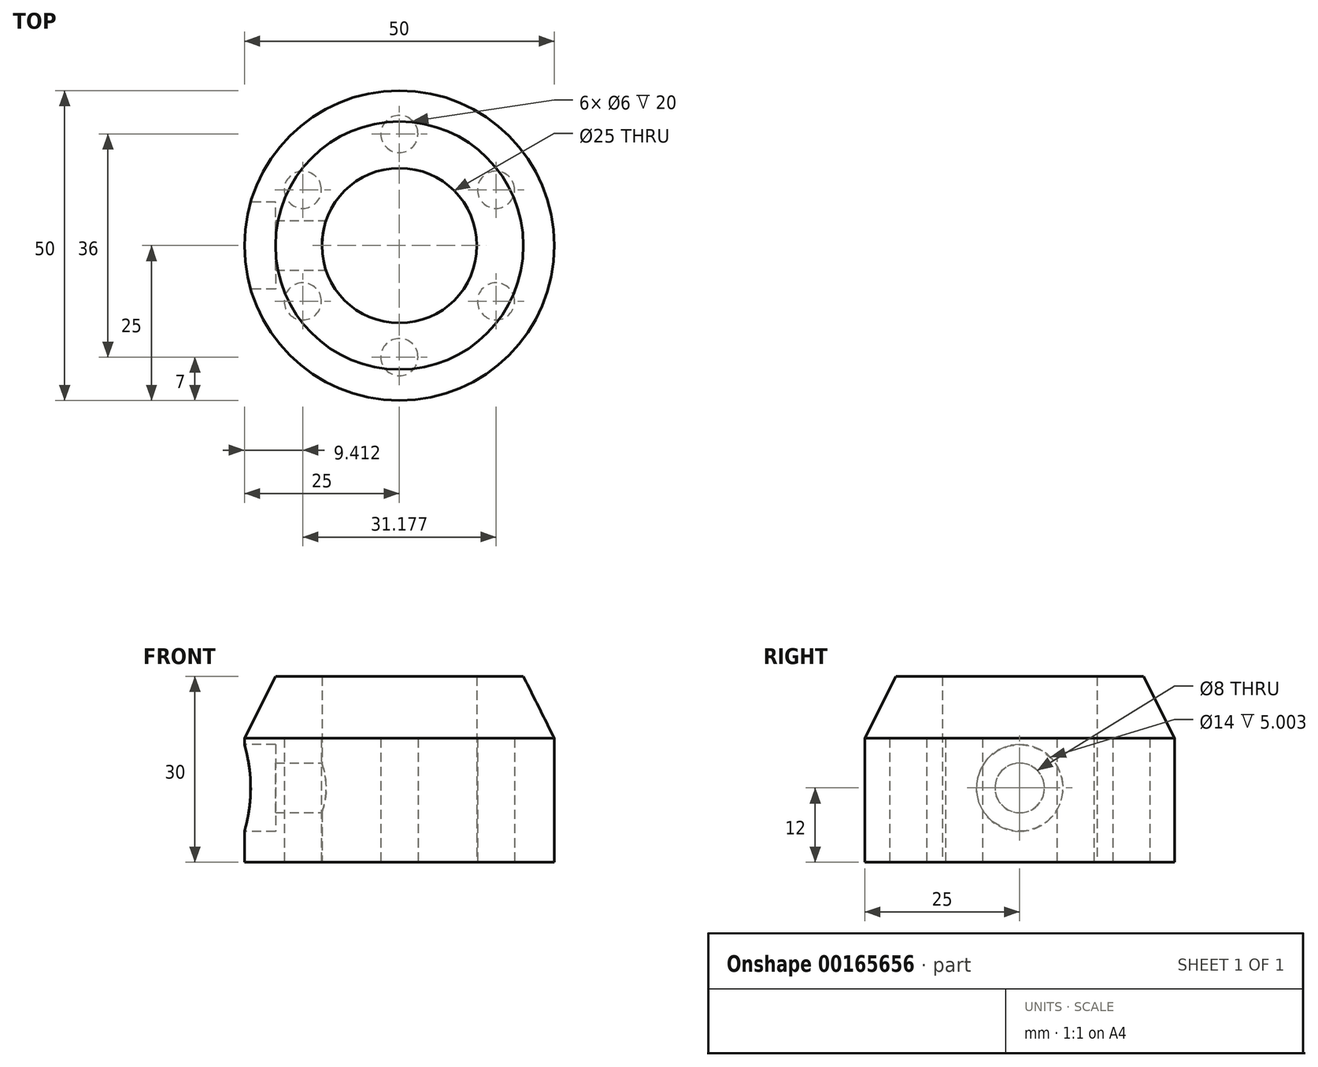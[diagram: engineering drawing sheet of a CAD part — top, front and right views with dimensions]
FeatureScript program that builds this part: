
annotation { "Feature Type Name" : "Feature", "Feature Type Description" : "" }
export const myFeature = defineFeature(function(context is Context, id is Id, definition is map)
    precondition{}
    {
        {
            var Q0;
            Q0=qCreatedBy(makeId("Top.planeOp"),FACE);
            var sketch = newSketch(context, id + "F0", { "sketchPlane" : qUnion([Q0])});
            skCircle(sketch, "E0", {"center": v(0, 0) * mm, "radius": 25 * mm});
            skCircle(sketch, "E1", {"center": v(0, 0) * mm, "radius": 12.5 * mm});
            skCircle(sketch, "E2", {"center": v(0, -18) * mm, "radius": 3 * mm});
            skCircle(sketch, "E3.1.0", {"center": v(15.59, -9) * mm, "radius": 3 * mm});
            skCircle(sketch, "E3.2.0", {"center": v(15.59, 9) * mm, "radius": 3 * mm});
            skCircle(sketch, "E3.3.0", {"center": v(0, 18) * mm, "radius": 3 * mm});
            skCircle(sketch, "E3.4.0", {"center": v(-15.59, 9) * mm, "radius": 3 * mm});
            skCircle(sketch, "E3.5.0", {"center": v(-15.59, -9) * mm, "radius": 3 * mm});
            skSolve(sketch);
        }
        {
            var Q0;
            Q0=makeQuery(id+"F0.imprint","IMPRINT",FACE,{"disambiguationData":[TD([[makeQuery(id+"F0.imprint","IMPRINT",EDGE,{"derivedFrom":sQuery(id+"F0.wireOp",EDGE,"E0")}),1.0]])]});
            var Q1;
            Q1=makeQuery(id+"F0.imprint","IMPRINT",FACE,{"disambiguationData":[TD([[makeQuery(id+"F0.imprint","IMPRINT",EDGE,{"derivedFrom":sQuery(id+"F0.wireOp",EDGE,"E2")}),1.0]])]});
            var Q2;
            Q2=makeQuery(id+"F0.imprint","IMPRINT",FACE,{"disambiguationData":[TD([[makeQuery(id+"F0.imprint","IMPRINT",EDGE,{"derivedFrom":sQuery(id+"F0.wireOp",EDGE,"E3.5.0")}),1.0]])]});
            var Q3;
            Q3=makeQuery(id+"F0.imprint","IMPRINT",FACE,{"disambiguationData":[TD([[makeQuery(id+"F0.imprint","IMPRINT",EDGE,{"derivedFrom":sQuery(id+"F0.wireOp",EDGE,"E3.1.0")}),1.0]])]});
            var Q4;
            Q4=makeQuery(id+"F0.imprint","IMPRINT",FACE,{"disambiguationData":[TD([[makeQuery(id+"F0.imprint","IMPRINT",EDGE,{"derivedFrom":sQuery(id+"F0.wireOp",EDGE,"E3.2.0")}),1.0]])]});
            var Q5;
            Q5=makeQuery(id+"F0.imprint","IMPRINT",FACE,{"disambiguationData":[TD([[makeQuery(id+"F0.imprint","IMPRINT",EDGE,{"derivedFrom":sQuery(id+"F0.wireOp",EDGE,"E3.3.0")}),1.0]])]});
            var Q6;
            Q6=makeQuery(id+"F0.imprint","IMPRINT",FACE,{"disambiguationData":[TD([[makeQuery(id+"F0.imprint","IMPRINT",EDGE,{"derivedFrom":sQuery(id+"F0.wireOp",EDGE,"E3.4.0")}),1.0]])]});
            extrude(context, id + "F1", {"entities" : qUnion([Q0, Q1, Q2, Q3, Q4, Q5, Q6]), "depth" : 20 * mm, "offsetDistance" : 25 * mm});
        }
        {
            var Q0;
            Q0=makeQuery(id+"F1.opExtrude","CAP_FACE",FACE,{"disambiguationData":[OSD([sQuery(id+"F0.wireOp",EDGE,"E0")])],"isStart":false});
            var sketch = newSketch(context, id + "F2", { "sketchPlane" : qUnion([Q0])});
            skCircle(sketch, "E4", {"center": v(0, 0) * mm, "radius": 25 * mm});
            skSolve(sketch);
        }
        {
            var Q0;
            Q0=makeQuery(id+"F2.imprint","IMPRINT",FACE,{"disambiguationData":[TD([[makeQuery(id+"F2.imprint","IMPRINT",EDGE,{"derivedFrom":sQuery(id+"F2.wireOp",EDGE,"E4")}),1.0]])]});
            extrude(context, id + "F3", {"entities" : qUnion([Q0]), "operationType" : NewBodyOperationType.ADD, "depth" : 10 * mm, "offsetDistance" : 25 * mm});
        }
        {
            var Q0;
            Q0=makeQuery(id+"F3.opExtrude","CAP_EDGE",EDGE,{"disambiguationData":[OSD([sQuery(id+"F2.wireOp",EDGE,"E4")])],"isStart":false});
            chamfer(context, id + "F4", {"entities" : qUnion([Q0]), "chamferType" : ChamferType.TWO_OFFSETS, "width1" : 5 * mm, "oppositeDirection" : false, "width2" : 10 * mm, "tangentPropagation" : true});
        }
        {
            var Q0;
            Q0=qCreatedBy(makeId("Right.planeOp"),FACE);
            var sketch = newSketch(context, id + "F5", { "sketchPlane" : qUnion([Q0])});
            skCircle(sketch, "E5", {"center": v(0, 12) * mm, "radius": 4 * mm});
            skSolve(sketch);
        }
        {
            var Q0;
            Q0=makeQuery(id+"F5.imprint","IMPRINT",FACE,{"disambiguationData":[TD([[makeQuery(id+"F5.imprint","IMPRINT",EDGE,{"derivedFrom":sQuery(id+"F5.wireOp",EDGE,"E5")}),1.0]])]});
            var Q1;
            Q1=makeQuery(id+"F3.boolean.opBoolean","MERGE",FACE,{"derivedFrom":[makeQuery(id+"F1.opExtrude","SWEPT_FACE",FACE,{"disambiguationData":[OSD([sQuery(id+"F0.wireOp",EDGE,"E0")])]}),makeQuery(id+"F3.opExtrude","SWEPT_FACE",FACE,{"disambiguationData":[OSD([sQuery(id+"F2.wireOp",EDGE,"E4")])]})]});
            extrude(context, id + "F6", {"entities" : qUnion([Q0]), "operationType" : NewBodyOperationType.REMOVE, "endBound" : BoundingType.UP_TO_SURFACE, "oppositeDirection" : true, "depth" : 25 * mm, "endBoundEntityFace" : qUnion([Q1]), "offsetDistance" : 25 * mm});
        }
        {
            var Q0;
            Q0=qCreatedBy(makeId("Right.planeOp"),FACE);
            cPlane(context, id + "F7", {"entities" : qUnion([Q0]), "cplaneType" : CPlaneType.OFFSET, "offset" : 25 * mm, "oppositeDirection" : true, "width" : 150 * mm, "height" : 150 * mm});
        }
        {
            var Q0;
            Q0=qCreatedBy(id+"F7.planeOp",FACE);
            var sketch = newSketch(context, id + "F8", { "sketchPlane" : qUnion([Q0])});
            skCircle(sketch, "E6", {"center": v(0, 12) * mm, "radius": 7 * mm});
            skSolve(sketch);
        }
        {
            var Q0;
            Q0=makeQuery(id+"F8.imprint","IMPRINT",FACE,{"disambiguationData":[TD([[makeQuery(id+"F8.imprint","IMPRINT",EDGE,{"derivedFrom":sQuery(id+"F8.wireOp",EDGE,"E6")}),1.0]])]});
            extrude(context, id + "F9", {"entities" : qUnion([Q0]), "operationType" : NewBodyOperationType.REMOVE, "depth" : 5 * mm, "offsetDistance" : 25 * mm});
        }
        {
            var Q0;
            Q0=makeQuery(id+"F0.imprint","IMPRINT",FACE,{"disambiguationData":[TD([[makeQuery(id+"F0.imprint","IMPRINT",EDGE,{"derivedFrom":sQuery(id+"F0.wireOp",EDGE,"E2")}),1.0]])]});
            var Q1;
            Q1=makeQuery(id+"F0.imprint","IMPRINT",FACE,{"disambiguationData":[TD([[makeQuery(id+"F0.imprint","IMPRINT",EDGE,{"derivedFrom":sQuery(id+"F0.wireOp",EDGE,"E3.1.0")}),1.0]])]});
            var Q2;
            Q2=makeQuery(id+"F0.imprint","IMPRINT",FACE,{"disambiguationData":[TD([[makeQuery(id+"F0.imprint","IMPRINT",EDGE,{"derivedFrom":sQuery(id+"F0.wireOp",EDGE,"E3.2.0")}),1.0]])]});
            var Q3;
            Q3=makeQuery(id+"F0.imprint","IMPRINT",FACE,{"disambiguationData":[TD([[makeQuery(id+"F0.imprint","IMPRINT",EDGE,{"derivedFrom":sQuery(id+"F0.wireOp",EDGE,"E3.3.0")}),1.0]])]});
            var Q4;
            Q4=makeQuery(id+"F0.imprint","IMPRINT",FACE,{"disambiguationData":[TD([[makeQuery(id+"F0.imprint","IMPRINT",EDGE,{"derivedFrom":sQuery(id+"F0.wireOp",EDGE,"E3.4.0")}),1.0]])]});
            var Q5;
            Q5=makeQuery(id+"F0.imprint","IMPRINT",FACE,{"disambiguationData":[TD([[makeQuery(id+"F0.imprint","IMPRINT",EDGE,{"derivedFrom":sQuery(id+"F0.wireOp",EDGE,"E3.5.0")}),1.0]])]});
            extrude(context, id + "F10", {"entities" : qUnion([Q0, Q1, Q2, Q3, Q4, Q5]), "operationType" : NewBodyOperationType.REMOVE, "depth" : 20 * mm, "offsetDistance" : 25 * mm});
        }
    });
